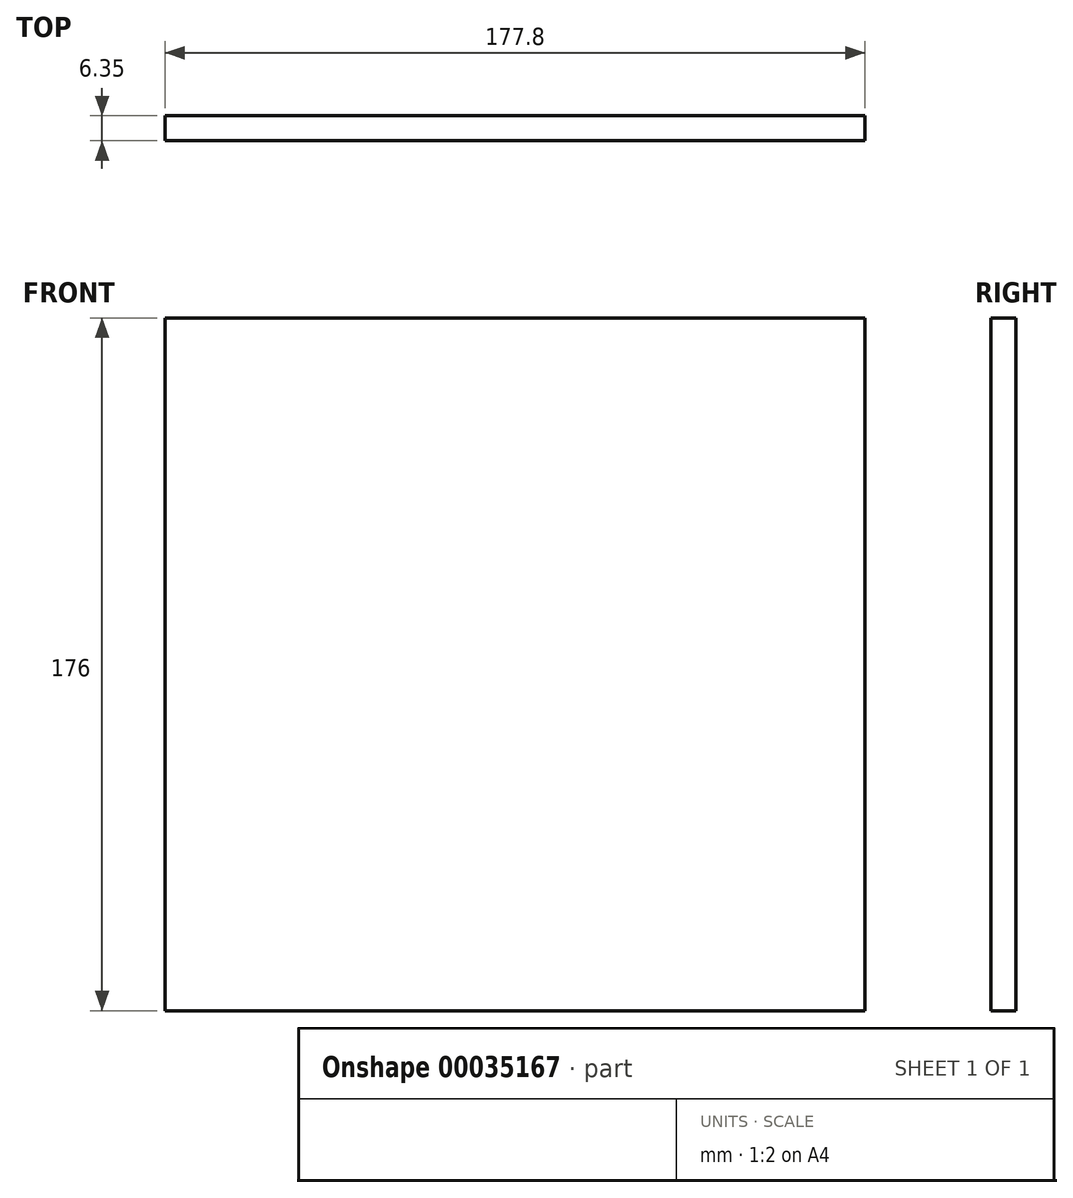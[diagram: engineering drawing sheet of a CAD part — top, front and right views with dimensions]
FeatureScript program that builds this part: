
annotation { "Feature Type Name" : "Feature", "Feature Type Description" : "" }
export const myFeature = defineFeature(function(context is Context, id is Id, definition is map)
    precondition{}
    {
        {
            var Q0;
            Q0=qCreatedBy(makeId("Front.planeOp"),FACE);
            var sketch = newSketch(context, id + "F0", { "sketchPlane" : qUnion([Q0])});
            skLineSegment(sketch, "E0.bottom", {"start": v(-98.97, 62.94) * mm, "end": v(78.83, 62.94) * mm});
            skLineSegment(sketch, "E0.top", {"start": v(-98.97, -113.06) * mm, "end": v(78.83, -113.06) * mm});
            skLineSegment(sketch, "E0.left", {"start": v(-98.97, 62.94) * mm, "end": v(-98.97, -113.06) * mm});
            skLineSegment(sketch, "E0.right", {"start": v(78.83, 62.94) * mm, "end": v(78.83, -113.06) * mm});
            skSolve(sketch);
        }
        {
            var Q0;
            Q0 = qSketchRegion(id + "F0", true);
            extrude(context, id + "F1", {"entities" : qUnion([Q0]), "depth" : 6.35 * mm});
        }
    });
